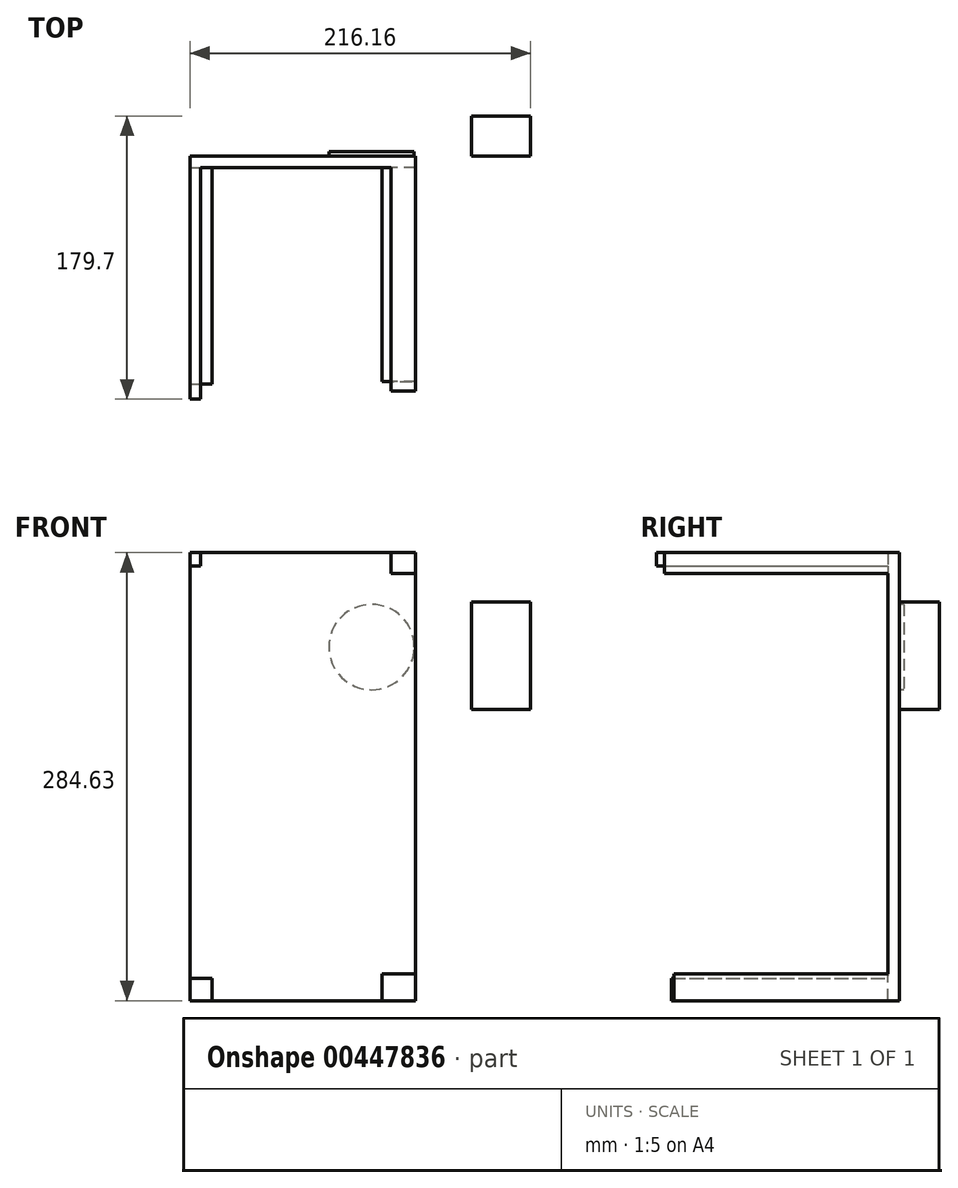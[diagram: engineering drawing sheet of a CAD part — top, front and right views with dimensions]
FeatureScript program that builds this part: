
annotation { "Feature Type Name" : "Feature", "Feature Type Description" : "" }
export const myFeature = defineFeature(function(context is Context, id is Id, definition is map)
    precondition{}
    {
        {
            var Q0;
            Q0=qCreatedBy(makeId("Front.planeOp"),FACE);
            var sketch = newSketch(context, id + "F0", { "sketchPlane" : qUnion([Q0])});
            skLineSegment(sketch, "E0.bottom", {"start": v(0, 144.47) * mm, "end": v(143.26, 144.47) * mm});
            skLineSegment(sketch, "E0.top", {"start": v(0, -140.16) * mm, "end": v(143.26, -140.16) * mm});
            skLineSegment(sketch, "E0.left", {"start": v(0, 144.47) * mm, "end": v(0, -140.16) * mm});
            skLineSegment(sketch, "E0.right", {"start": v(143.26, 144.47) * mm, "end": v(143.26, -140.16) * mm});
            skSolve(sketch);
        }
        {
            var Q0;
            Q0=makeQuery(id+"F0.imprint","IMPRINT",FACE,{"disambiguationData":[TD([[makeQuery(id+"F0.imprint","IMPRINT",EDGE,{"derivedFrom":sQuery(id+"F0.wireOp",EDGE,"E0.bottom")}),-1.0]])]});
            extrude(context, id + "F1", {"entities" : qUnion([Q0]), "depth" : 7.2 * mm});
        }
        {
            var Q0;
            Q0=makeQuery(id+"F1.opExtrude","CAP_FACE",FACE,{"disambiguationData":[OSD([sQuery(id+"F0.wireOp",EDGE,"E0.bottom"),sQuery(id+"F0.wireOp",EDGE,"E0.top"),sQuery(id+"F0.wireOp",EDGE,"E0.left"),sQuery(id+"F0.wireOp",EDGE,"E0.right")])],"isStart":false});
            var sketch = newSketch(context, id + "F2", { "sketchPlane" : qUnion([Q0])});
            skLineSegment(sketch, "E1.bottom", {"start": v(0, -140.16) * mm, "end": v(13.89, -140.16) * mm});
            skLineSegment(sketch, "E1.top", {"start": v(0, -126.08) * mm, "end": v(13.89, -126.08) * mm});
            skLineSegment(sketch, "E1.left", {"start": v(0, -140.16) * mm, "end": v(0, -126.08) * mm});
            skLineSegment(sketch, "E1.right", {"start": v(13.89, -140.16) * mm, "end": v(13.89, -126.08) * mm});
            skSolve(sketch);
        }
        {
            var Q0;
            Q0 = qSketchRegion(id + "F2", true);
            extrude(context, id + "F3", {"entities" : qUnion([Q0]), "operationType" : NewBodyOperationType.ADD, "depth" : 137.5 * mm});
        }
        {
            var Q0;
            Q0=makeQuery(id+"F1.opExtrude","CAP_FACE",FACE,{"disambiguationData":[OSD([sQuery(id+"F0.wireOp",EDGE,"E0.bottom"),sQuery(id+"F0.wireOp",EDGE,"E0.top"),sQuery(id+"F0.wireOp",EDGE,"E0.left"),sQuery(id+"F0.wireOp",EDGE,"E0.right")])],"isStart":false});
            var sketch = newSketch(context, id + "F4", { "sketchPlane" : qUnion([Q0])});
            skLineSegment(sketch, "E2.bottom", {"start": v(143.26, -140.16) * mm, "end": v(122, -140.16) * mm});
            skLineSegment(sketch, "E2.top", {"start": v(143.26, -123.22) * mm, "end": v(122, -123.22) * mm});
            skLineSegment(sketch, "E2.left", {"start": v(143.26, -140.16) * mm, "end": v(143.26, -123.22) * mm});
            skLineSegment(sketch, "E2.right", {"start": v(122, -140.16) * mm, "end": v(122, -123.22) * mm});
            skSolve(sketch);
        }
        {
            var Q0;
            Q0 = qSketchRegion(id + "F4", true);
            extrude(context, id + "F5", {"entities" : qUnion([Q0]), "operationType" : NewBodyOperationType.ADD, "depth" : 136 * mm});
        }
        {
            var Q0;
            Q0=makeQuery(id+"F1.opExtrude","CAP_FACE",FACE,{"disambiguationData":[OSD([sQuery(id+"F0.wireOp",EDGE,"E0.bottom"),sQuery(id+"F0.wireOp",EDGE,"E0.top"),sQuery(id+"F0.wireOp",EDGE,"E0.left"),sQuery(id+"F0.wireOp",EDGE,"E0.right")])],"isStart":false});
            var sketch = newSketch(context, id + "F6", { "sketchPlane" : qUnion([Q0])});
            skLineSegment(sketch, "E3.bottom", {"start": v(143.26, 144.47) * mm, "end": v(127.57, 144.47) * mm});
            skLineSegment(sketch, "E3.top", {"start": v(143.26, 131.14) * mm, "end": v(127.57, 131.14) * mm});
            skLineSegment(sketch, "E3.left", {"start": v(143.26, 144.47) * mm, "end": v(143.26, 131.14) * mm});
            skLineSegment(sketch, "E3.right", {"start": v(127.57, 144.47) * mm, "end": v(127.57, 131.14) * mm});
            skSolve(sketch);
        }
        {
            var Q0;
            Q0 = qSketchRegion(id + "F6", true);
            extrude(context, id + "F7", {"entities" : qUnion([Q0]), "operationType" : NewBodyOperationType.ADD, "depth" : 142.02 * mm});
        }
        {
            var Q0;
            Q0=makeQuery(id+"F1.opExtrude","CAP_FACE",FACE,{"disambiguationData":[OSD([sQuery(id+"F0.wireOp",EDGE,"E0.bottom"),sQuery(id+"F0.wireOp",EDGE,"E0.top"),sQuery(id+"F0.wireOp",EDGE,"E0.left"),sQuery(id+"F0.wireOp",EDGE,"E0.right")])],"isStart":false});
            var sketch = newSketch(context, id + "F8", { "sketchPlane" : qUnion([Q0])});
            skLineSegment(sketch, "E4.bottom", {"start": v(0, 144.47) * mm, "end": v(6.78, 144.47) * mm});
            skLineSegment(sketch, "E4.top", {"start": v(0, 136.09) * mm, "end": v(6.78, 136.09) * mm});
            skLineSegment(sketch, "E4.left", {"start": v(0, 144.47) * mm, "end": v(0, 136.09) * mm});
            skLineSegment(sketch, "E4.right", {"start": v(6.78, 144.47) * mm, "end": v(6.78, 136.09) * mm});
            skSolve(sketch);
        }
        {
            var Q0;
            Q0 = qSketchRegion(id + "F8", true);
            extrude(context, id + "F9", {"entities" : qUnion([Q0]), "operationType" : NewBodyOperationType.ADD, "depth" : 147.1 * mm});
        }
        {
            var Q0;
            Q0=makeQuery(id+"F1.opExtrude","CAP_FACE",FACE,{"disambiguationData":[OSD([sQuery(id+"F0.wireOp",EDGE,"E0.bottom"),sQuery(id+"F0.wireOp",EDGE,"E0.top"),sQuery(id+"F0.wireOp",EDGE,"E0.left"),sQuery(id+"F0.wireOp",EDGE,"E0.right")])],"isStart":true});
            var sketch = newSketch(context, id + "F10", { "sketchPlane" : qUnion([Q0])});
            skCircle(sketch, "E5", {"center": v(-115.24, 84.44) * mm, "radius": 27.1 * mm});
            skSolve(sketch);
        }
        {
            var Q0;
            Q0 = qSketchRegion(id + "F10", true);
            extrude(context, id + "F11", {"entities" : qUnion([Q0]), "operationType" : NewBodyOperationType.ADD, "depth" : 2.91 * mm});
        }
        {
            var Q0;
            Q0=makeQuery(id+"F1.opExtrude","CAP_FACE",FACE,{"disambiguationData":[OSD([sQuery(id+"F0.wireOp",EDGE,"E0.bottom"),sQuery(id+"F0.wireOp",EDGE,"E0.top"),sQuery(id+"F0.wireOp",EDGE,"E0.left"),sQuery(id+"F0.wireOp",EDGE,"E0.right")])],"isStart":true});
            var sketch = newSketch(context, id + "F12", { "sketchPlane" : qUnion([Q0])});
            skLineSegment(sketch, "E6.bottom", {"start": v(-178.83, 113) * mm, "end": v(-216.16, 113) * mm});
            skLineSegment(sketch, "E6.top", {"start": v(-178.83, 44.9) * mm, "end": v(-216.16, 44.9) * mm});
            skLineSegment(sketch, "E6.left", {"start": v(-178.83, 113) * mm, "end": v(-178.83, 44.9) * mm});
            skLineSegment(sketch, "E6.right", {"start": v(-216.16, 113) * mm, "end": v(-216.16, 44.9) * mm});
            skSolve(sketch);
        }
        {
            var Q0;
            Q0=makeQuery(id+"F12.imprint","IMPRINT",FACE,{"disambiguationData":[TD([[makeQuery(id+"F12.imprint","IMPRINT",EDGE,{"derivedFrom":sQuery(id+"F12.wireOp",EDGE,"E6.bottom")}),1.0]])]});
            var sketch = newSketch(context, id + "F13", { "sketchPlane" : qUnion([Q0])});
            skSolve(sketch);
        }
        {
            var Q0;
            Q0=makeQuery(id+"F13.imprint","IMPRINT",FACE,{"disambiguationData":[TD([[makeQuery(id+"F13.imprint","IMPRINT",EDGE,{"derivedFrom":makeQuery(id+"F12.imprint","IMPRINT",EDGE,{"derivedFrom":sQuery(id+"F12.wireOp",EDGE,"E6.bottom")})}),1.0]])]});
            var sketch = newSketch(context, id + "F14", { "sketchPlane" : qUnion([Q0])});
            skSolve(sketch);
        }
        {
            var Q0;
            Q0 = qSketchRegion(id + "F14", true);
            var Q1;
            Q1=makeQuery(id+"F13.imprint","IMPRINT",FACE,{"disambiguationData":[TD([[makeQuery(id+"F13.imprint","IMPRINT",EDGE,{"derivedFrom":makeQuery(id+"F12.imprint","IMPRINT",EDGE,{"derivedFrom":sQuery(id+"F12.wireOp",EDGE,"E6.bottom")})}),1.0]])]});
            extrude(context, id + "F15", {"entities" : qUnion([Q0, Q1]), "depth" : 25.4 * mm});
        }
    });
